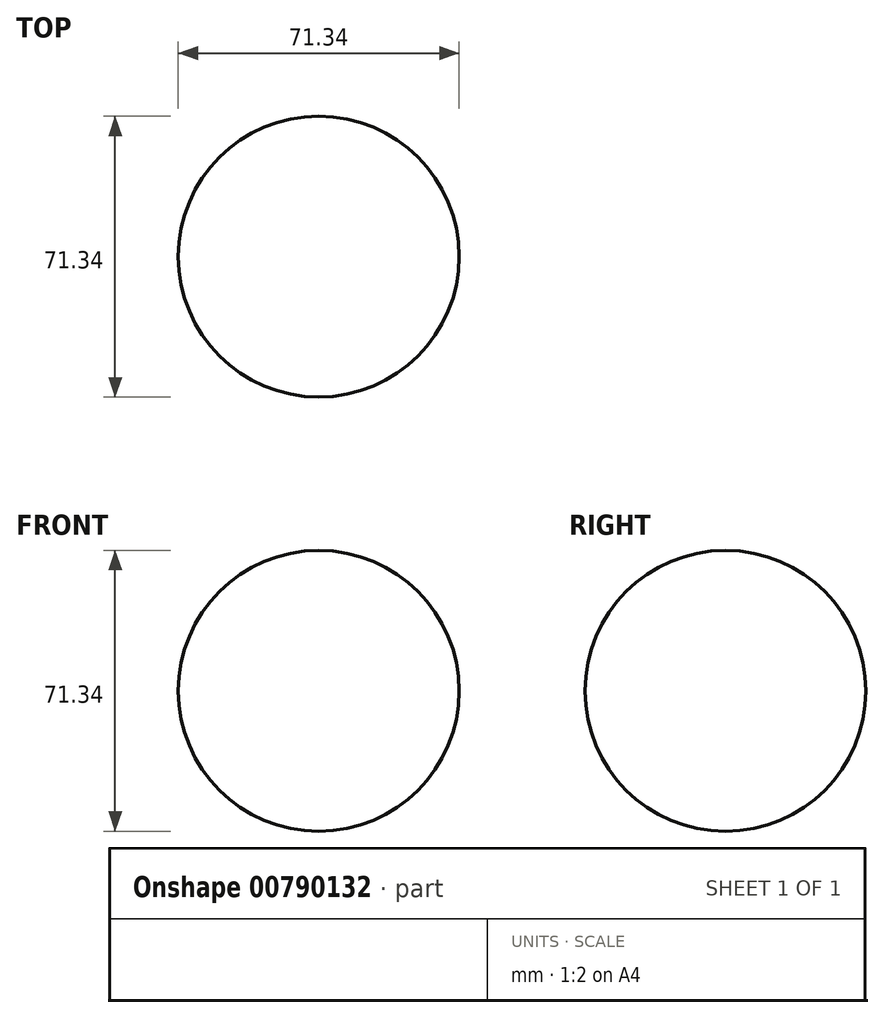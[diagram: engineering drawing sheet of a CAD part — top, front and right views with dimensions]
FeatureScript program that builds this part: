
annotation { "Feature Type Name" : "Feature", "Feature Type Description" : "" }
export const myFeature = defineFeature(function(context is Context, id is Id, definition is map)
    precondition{}
    {
        {
            var Q0;
            Q0=qCreatedBy(makeId("Top.planeOp"),FACE);
            var sketch = newSketch(context, id + "F0", { "sketchPlane" : qUnion([Q0])});
            skArc(sketch, "E0", {"start": v(0, -35.67) * mm, "mid": v(35.67, 0) * mm, "end": v(0, 35.67) * mm});
            skLineSegment(sketch, "E1", {"start": v(0, 35.67) * mm, "end": v(0, -35.67) * mm});
            skSolve(sketch);
        }
        {
            var Q0;
            Q0=makeQuery(id+"F0.imprint","IMPRINT",FACE,{"disambiguationData":[TD([[makeQuery(id+"F0.imprint","IMPRINT",EDGE,{"derivedFrom":sQuery(id+"F0.wireOp",EDGE,"E0")}),1.0]])]});
            var Q1;
            Q1=sQuery(id+"F0.wireOp",EDGE,"E1");
            revolve(context, id + "F1", {"surfaceOperationType" : NewSurfaceOperationType.NEW, "entities" : qUnion([Q0]), "axis" : qUnion([Q1]), "revolveType" : RevolveType.FULL});
        }
    });
